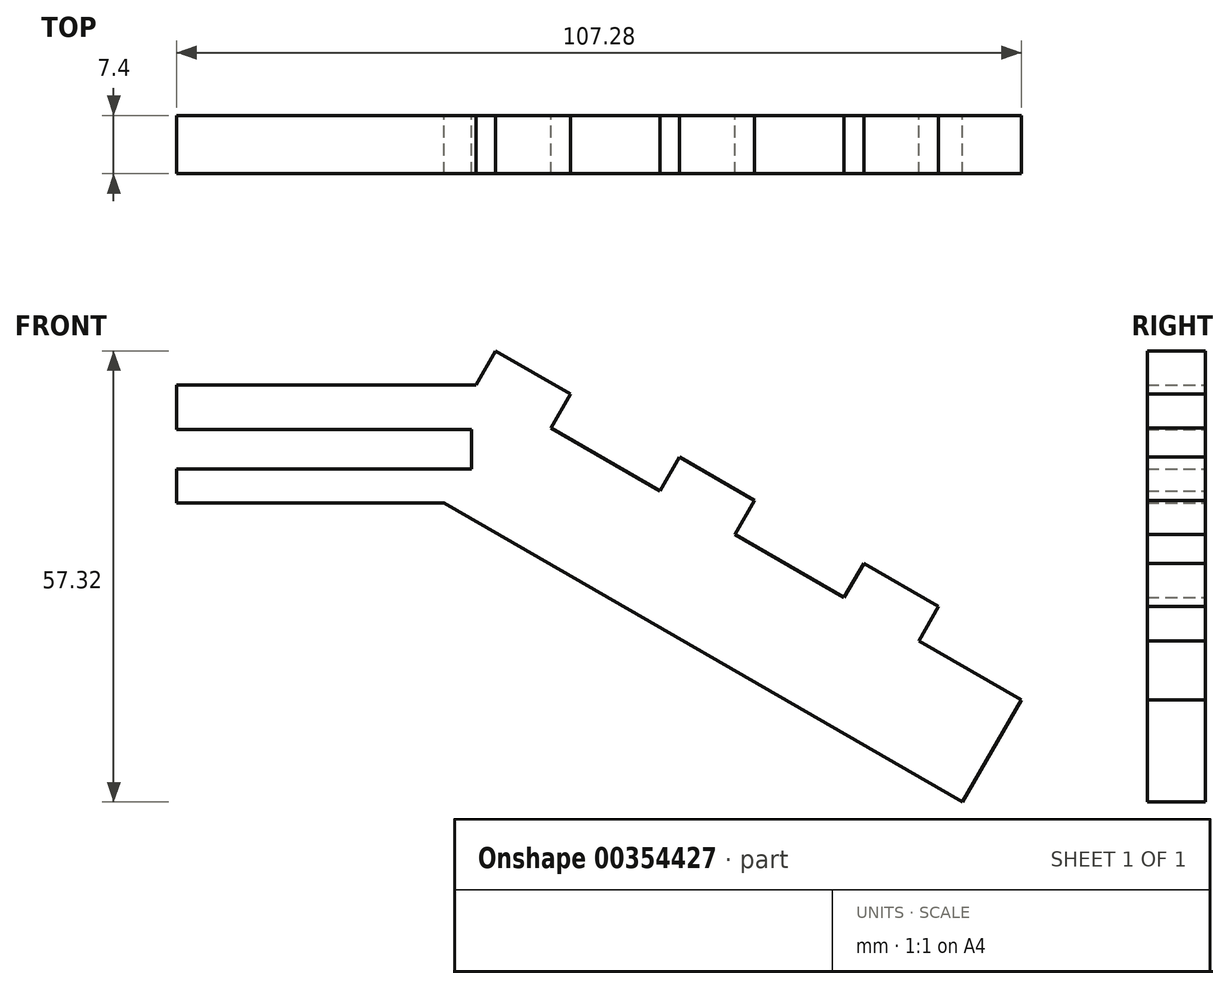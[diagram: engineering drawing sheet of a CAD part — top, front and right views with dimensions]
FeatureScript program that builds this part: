
annotation { "Feature Type Name" : "Feature", "Feature Type Description" : "" }
export const myFeature = defineFeature(function(context is Context, id is Id, definition is map)
    precondition{}
    {
        {
            var Q0;
            Q0=qCreatedBy(makeId("Front.planeOp"),FACE);
            var sketch = newSketch(context, id + "F0", { "sketchPlane" : qUnion([Q0])});
            skLineSegment(sketch, "E0", {"start": v(0, 15) * mm, "end": v(38, 15) * mm});
            skLineSegment(sketch, "E1", {"start": v(47.53, 9.5) * mm, "end": v(61.38, 1.5) * mm});
            skLineSegment(sketch, "E2", {"start": v(38, 15) * mm, "end": v(40.5, 19.33) * mm});
            skLineSegment(sketch, "E3", {"start": v(40.5, 19.33) * mm, "end": v(50.03, 13.83) * mm});
            skLineSegment(sketch, "E4", {"start": v(50.03, 13.83) * mm, "end": v(47.53, 9.5) * mm});
            skLineSegment(sketch, "E5.1.0.0", {"start": v(61.38, 1.5) * mm, "end": v(63.88, 5.83) * mm});
            skLineSegment(sketch, "E5.1.0.1", {"start": v(63.88, 5.83) * mm, "end": v(73.4, 0.33) * mm});
            skLineSegment(sketch, "E5.1.0.2", {"start": v(73.4, 0.33) * mm, "end": v(70.9, -4) * mm});
            skLineSegment(sketch, "E5.2.0.0", {"start": v(84.77, -12) * mm, "end": v(87.27, -7.67) * mm});
            skLineSegment(sketch, "E5.2.0.1", {"start": v(87.27, -7.67) * mm, "end": v(96.8, -13.17) * mm});
            skLineSegment(sketch, "E5.2.0.2", {"start": v(96.8, -13.17) * mm, "end": v(94.3, -17.5) * mm});
            skLineSegment(sketch, "E5.direction1", {"start": v(47.53, 9.5) * mm, "end": v(61.38, 1.5) * mm, "construction": true});
            skLineSegment(sketch, "E6", {"start": v(107.28, -25) * mm, "end": v(99.78, -38) * mm});
            skLineSegment(sketch, "E7", {"start": v(99.78, -38) * mm, "end": v(33.98, 0) * mm});
            skLineSegment(sketch, "E8", {"start": v(33.98, 0) * mm, "end": v(0, 0) * mm});
            skLineSegment(sketch, "E9", {"start": v(0, 0) * mm, "end": v(0, 4.35) * mm});
            skLineSegment(sketch, "E10", {"start": v(0, 4.35) * mm, "end": v(37.43, 4.35) * mm});
            skLineSegment(sketch, "E11", {"start": v(37.43, 4.35) * mm, "end": v(37.43, 9.35) * mm});
            skLineSegment(sketch, "E12", {"start": v(37.43, 9.35) * mm, "end": v(0, 9.35) * mm});
            skLineSegment(sketch, "E13.trimOffspring", {"start": v(0, 9.35) * mm, "end": v(0, 15) * mm});
            skLineSegment(sketch, "E14.trimOffspring", {"start": v(70.9, -4) * mm, "end": v(84.77, -12) * mm});
            skLineSegment(sketch, "E15.trimOffspring", {"start": v(94.3, -17.5) * mm, "end": v(107.28, -25) * mm});
            skSolve(sketch);
        }
        {
            var Q0;
            Q0 = qSketchRegion(id + "F0", true);
            extrude(context, id + "F1", {"entities" : qUnion([Q0]), "depth" : 7.4 * mm});
        }
    });
